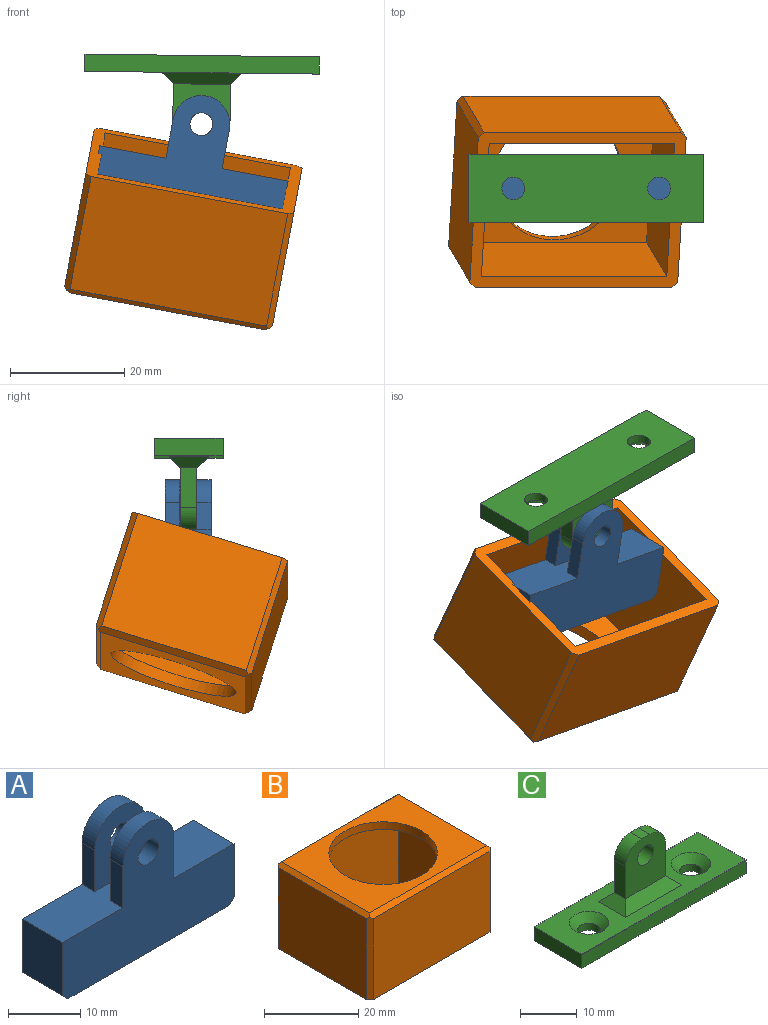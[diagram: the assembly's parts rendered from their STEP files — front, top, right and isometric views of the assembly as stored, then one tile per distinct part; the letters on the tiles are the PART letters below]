
ASSEMBLY  parts=3 mates=2
PART A: 18 faces, bbox 33.5x8x22 mm
  f0: plane 7x2.5mm, normal (1,0,0), area 17.5mm2, adj f3,f5,f13,f14
  f1: plane 7x2.5mm, normal (-1,0,0), area 17.5mm2, adj f3,f5,f13,f14
  f2: plane 33.5x22mm, normal (0,1,0), area 430.7mm2, adj f4,f5,f6,f7,f8,f9,f10,f11
  f3: plane 33.5x22mm, normal (0,-1,0), area 430.7mm2, adj f0,f1,f4,f5,f6,f8,f10,f11
  f4: plane 9x8mm, normal (1,0,0), area 72mm2, adj f2,f3,f5,f11
  f5: plane 33.5x8mm, normal (0,0,1), area 218mm2, adj f0,f1,f2,f3,f4,f7,f8,f9
  f6: plane 31.5x8mm, normal (0,0,-1), area 252mm2, adj f2,f3,f10,f11
  f7: plane 7x2.5mm, normal (1,0,0), area 17.5mm2, adj f2,f5,f12,f15
  f8: plane 9x8mm, normal (-1,0,0), area 72mm2, adj f2,f3,f5,f10
  f9: plane 7x2.5mm, normal (-1,0,0), area 17.5mm2, adj f2,f5,f12,f15
  f10: plane 8x1mm, normal (-0.71,0,-0.71), area 11.3mm2, adj f2,f3,f6,f8
  f11: plane 8x1mm, normal (0.71,0,-0.71), area 11.3mm2, adj f2,f3,f4,f6
  f12: plane 12x10mm, normal (0,-1,0), area 96.7mm2, adj f5,f7,f9,f15,f17
  f13: plane 12x10mm, normal (0,1,0), area 96.7mm2, adj f0,f1,f5,f14,f16
  f14: cylinder r=5mm len=10mm, axis (0,1,0), area 39.3mm2, adj f0,f1,f3,f13
  f15: cylinder r=5mm len=10mm, axis (0,-1,0), area 39.3mm2, adj f2,f7,f9,f12
  f16: cylinder r=2mm len=4mm, axis (0,-1,0), area 31.4mm2, adj f3,f13
  f17: cylinder r=2mm len=4mm, axis (0,-1,0), area 31.4mm2, adj f2,f12
PART B: 20 faces, bbox 37x28.5x22 mm
  f0: plane 35x21mm, normal (0,1,0), area 735mm2, adj f5,f7,f10,f12
  f1: plane 26.5x21mm, normal (-1,0,0), area 556.5mm2, adj f5,f9,f10,f11
  f2: plane 35x21mm, normal (0,-1,0), area 735mm2, adj f5,f8,f11,f13
  f3: plane 26.5x21mm, normal (1,0,0), area 556.5mm2, adj f5,f6,f12,f13
  f4: plane 35x26.5mm, normal (0,0,1), area 512mm2, adj f6,f7,f8,f9,f19
  f5: plane 37x28.5mm, normal (0,0,-1), area 244mm2, adj f0,f1,f2,f3,f10,f11,f12,f13
  f6: plane 27.5x1mm, normal (0.71,0,0.71), area 38.2mm2, adj f3,f4,f7,f8,f12,f13
  f7: plane 36x1mm, normal (0,0.71,0.71), area 50.2mm2, adj f0,f4,f6,f9,f10,f12
  f8: plane 36x1mm, normal (0,-0.71,0.71), area 50.2mm2, adj f2,f4,f6,f9,f11,f13
  f9: plane 27.5x1mm, normal (-0.71,0,0.71), area 38.2mm2, adj f1,f4,f7,f8,f10,f11
  f10: plane 21.5x1mm, normal (-0.71,0.71,0), area 30.1mm2, adj f0,f1,f5,f7,f9
  f11: plane 21.5x1mm, normal (-0.71,-0.71,0), area 30.1mm2, adj f1,f2,f5,f8,f9
  f12: plane 21.5x1mm, normal (0.71,0.71,0), area 30.1mm2, adj f0,f3,f5,f6,f7
  f13: plane 21.5x1mm, normal (0.71,-0.71,0), area 30.1mm2, adj f2,f3,f5,f6,f8
  f14: plane 33x24.5mm, normal (0,0,-1), area 393mm2, adj f15,f16,f17,f18,f19
  f15: plane 33x20mm, normal (0,-1,0), area 660mm2, adj f5,f14,f16,f18
  f16: plane 24.5x20mm, normal (1,0,0), area 490mm2, adj f5,f14,f15,f17
  f17: plane 33x20mm, normal (0,1,0), area 660mm2, adj f5,f14,f16,f18
  f18: plane 24.5x20mm, normal (-1,0,0), area 490mm2, adj f5,f14,f15,f17
  f19: cylinder r=11.5mm len=23mm, axis (0,0,1), area 144.5mm2, adj f4,f14
PART C: 22 faces, bbox 41x12x16 mm
  f0: plane 7x2.8mm, normal (-1,0,0), area 19.6mm2, adj f6,f15,f16,f18
  f1: plane 7x2.8mm, normal (1,0,0), area 19.6mm2, adj f5,f15,f16,f19
  f2: plane 2.8x2mm, normal (0,0,1), area 5.6mm2, adj f5,f6,f15,f16
  f3: plane 41x3mm, normal (0,-1,0), area 123mm2, adj f7,f9,f10,f11
  f4: plane 41x3mm, normal (0,1,0), area 123mm2, adj f7,f9,f10,f11
  f5: cylinder r=4mm len=4mm, axis (0,-1,0), area 17.6mm2, adj f1,f2,f15,f16
  f6: cylinder r=4mm len=4mm, axis (0,1,0), area 17.6mm2, adj f0,f2,f15,f16
  f7: plane 12x3mm, normal (-1,0,0), area 36mm2, adj f3,f4,f9,f10
  f8: cylinder r=2mm len=4mm, axis (0,0,-1), area 18.8mm2, adj f10,f13
  f9: plane 41x12mm, normal (0,0,1), area 319.8mm2, adj f3,f4,f7,f11,f13,f14,f18,f19
  f10: plane 41x12mm, normal (0,0,-1), area 466.9mm2, adj f3,f4,f7,f8,f11,f12
  f11: plane 12x3mm, normal (1,0,0), area 36mm2, adj f3,f4,f9,f10
  f12: cylinder r=2mm len=4mm, axis (0,0,-1), area 18.8mm2, adj f10,f14
  f13: cone r=2mm half-angle=45deg, axis (0,0,1), area 36.7mm2, adj f8,f9
  f14: cone r=2mm half-angle=45deg, axis (0,0,1), area 36.7mm2, adj f9,f12
  f15: plane 11x10mm, normal (0,-1,0), area 90.6mm2, adj f0,f1,f2,f5,f6,f17,f21
  f16: plane 11x10mm, normal (0,1,0), area 90.6mm2, adj f0,f1,f2,f5,f6,f17,f20
  f17: cylinder r=2mm len=4mm, axis (0,1,0), area 35.2mm2, adj f15,f16
  f18: plane 6.8x2mm, normal (-0.71,0,0.71), area 13.6mm2, adj f0,f9,f20,f21
  f19: plane 6.8x2mm, normal (0.71,0,0.71), area 13.6mm2, adj f1,f9,f20,f21
  f20: plane 14x2mm, normal (0,0.71,0.71), area 33.9mm2, adj f9,f16,f18,f19
  f21: plane 14x2mm, normal (0,-0.71,0.71), area 33.9mm2, adj f9,f15,f18,f19
PLACE A rot(axis=(0,1,0),10.7deg) t=(-19.23,-5.29,-0.86)mm
PLACE B rot(axis=(-1,0.01,0.09),162.6deg) t=(38.13,-7.2,-7.02)mm
PLACE C rot(axis=(-1,0,0.01),180deg) t=(39.3,23.44,21.98)mm
MATE cylindrical A.f14 <-> C.f17  axis (0,1,0) through (13.46,8.23,10.28)mm
MATE planar A.f4 <-> B.f18  axis (0.98,0,-0.19) through (28.63,9.73,0.3)mm
